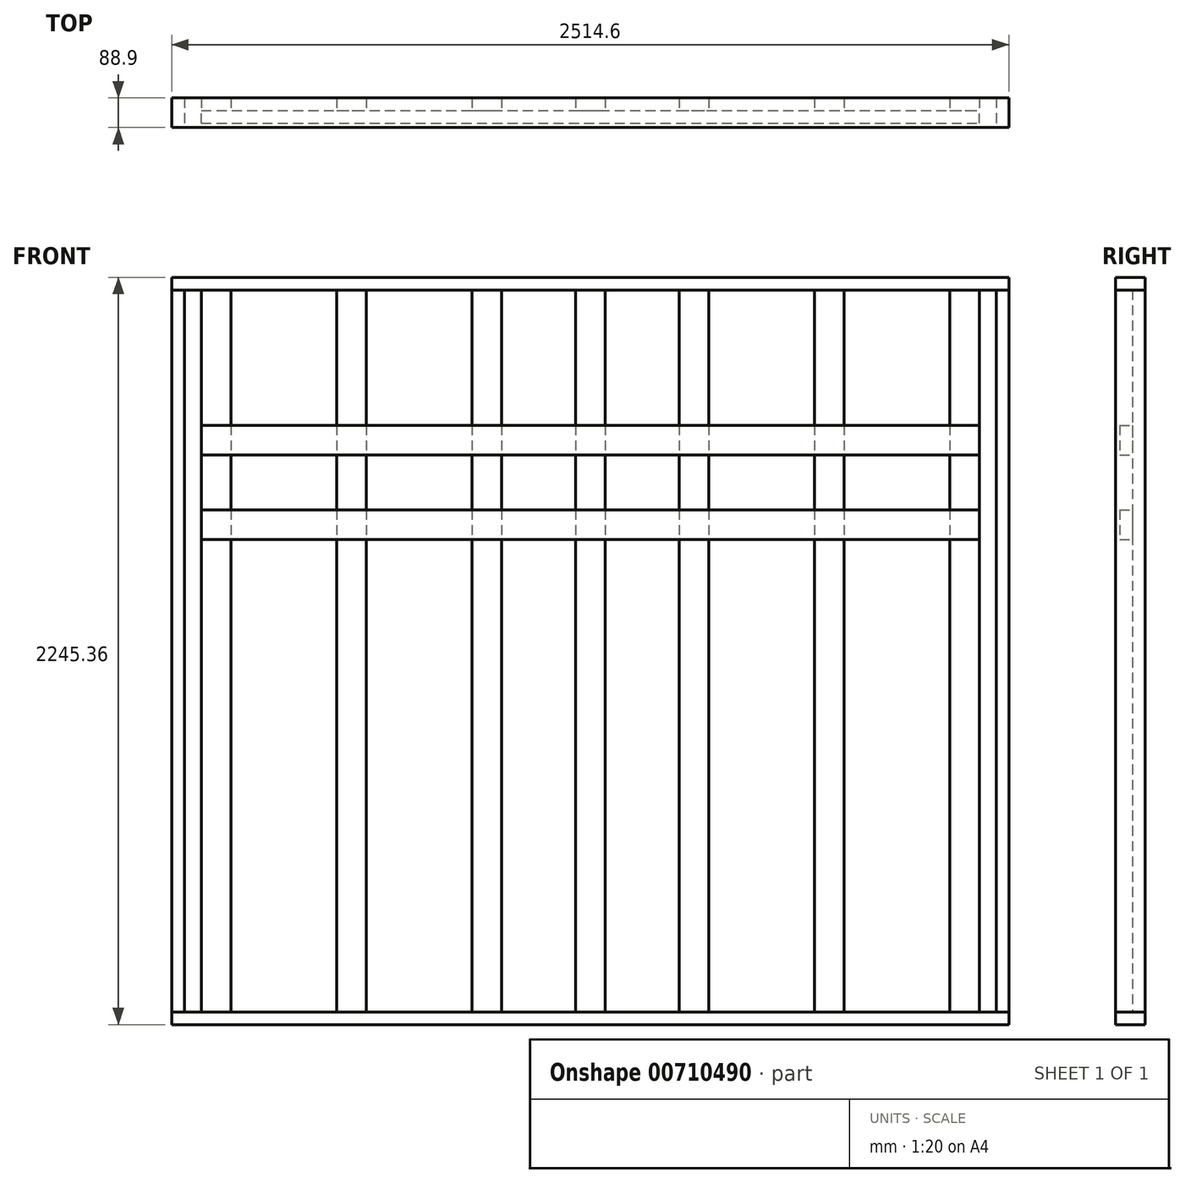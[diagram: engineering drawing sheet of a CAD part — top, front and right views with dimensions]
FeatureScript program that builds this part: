
annotation { "Feature Type Name" : "Feature", "Feature Type Description" : "" }
export const myFeature = defineFeature(function(context is Context, id is Id, definition is map)
    precondition{}
    {
        {
            var Q0;
            Q0=qCreatedBy(makeId("Top.planeOp"),FACE);
            var sketch = newSketch(context, id + "F0", { "sketchPlane" : qUnion([Q0])});
            skLineSegment(sketch, "E0.bottom", {"start": v(1257.3, 44.45) * mm, "end": v(-1257.3, 44.45) * mm});
            skLineSegment(sketch, "E0.top", {"start": v(1257.3, -44.45) * mm, "end": v(-1257.3, -44.45) * mm});
            skLineSegment(sketch, "E0.left", {"start": v(1257.3, 44.45) * mm, "end": v(1257.3, -44.45) * mm});
            skLineSegment(sketch, "E0.right", {"start": v(-1257.3, 44.45) * mm, "end": v(-1257.3, -44.45) * mm});
            skPoint(sketch, "E0.middle", {"position": v(0, 0) * mm});
            skSolve(sketch);
        }
        {
            var Q0;
            Q0=qSketchRegion(id+"F0",true);
            extrude(context, id + "F1", {"entities" : qUnion([Q0]), "depth" : 38.1 * mm, "offsetDistance" : 25.4 * mm});
        }
        {
            var Q0;
            Q0=makeQuery(id+"F1.opExtrude","CAP_FACE",FACE,{"disambiguationData":[OSD([sQuery(id+"F0.wireOp",EDGE,"E0.bottom"),sQuery(id+"F0.wireOp",EDGE,"E0.top"),sQuery(id+"F0.wireOp",EDGE,"E0.left"),sQuery(id+"F0.wireOp",EDGE,"E0.right")])],"isStart":false});
            var sketch = newSketch(context, id + "F2", { "sketchPlane" : qUnion([Q0])});
            skLineSegment(sketch, "E1.bottom", {"start": v(-1257.3, 44.45) * mm, "end": v(-1219.2, 44.45) * mm});
            skLineSegment(sketch, "E1.top", {"start": v(-1257.3, -44.45) * mm, "end": v(-1219.2, -44.45) * mm});
            skLineSegment(sketch, "E1.left", {"start": v(-1257.3, 44.45) * mm, "end": v(-1257.3, -44.45) * mm});
            skLineSegment(sketch, "E1.right", {"start": v(-1219.2, 44.45) * mm, "end": v(-1219.2, -44.45) * mm});
            skSolve(sketch);
        }
        {
            var Q0;
            Q0=makeQuery(id+"F2.imprint","IMPRINT",FACE,{"disambiguationData":[TD([[makeQuery(id+"F2.imprint","IMPRINT",EDGE,{"derivedFrom":sQuery(id+"F2.wireOp",EDGE,"E1.bottom")}),1.0]])]});
            extrude(context, id + "F3", {"entities" : qUnion([Q0]), "depth" : 2169.16 * mm, "offsetDistance" : 25.4 * mm});
        }
        {
            var Q0;
            Q0=makeQuery(id+"F3.opExtrude","SWEPT_BODY",BODY,{"disambiguationData":[OSD([sQuery(id+"F2.wireOp",EDGE,"E1.bottom"),sQuery(id+"F2.wireOp",EDGE,"E1.top"),sQuery(id+"F2.wireOp",EDGE,"E1.left"),sQuery(id+"F2.wireOp",EDGE,"E1.right")])]});
            var Q1;
            Q1=qCreatedBy(makeId("Right.planeOp"),FACE);
            mirror(context, id + "F4", {"entities" : qUnion([Q0]), "mirrorPlane" : qUnion([Q1])});
        }
        {
            var Q0;
            Q0=makeQuery(id+"F1.opExtrude","CAP_FACE",FACE,{"disambiguationData":[OSD([sQuery(id+"F0.wireOp",EDGE,"E0.bottom"),sQuery(id+"F0.wireOp",EDGE,"E0.top"),sQuery(id+"F0.wireOp",EDGE,"E0.left"),sQuery(id+"F0.wireOp",EDGE,"E0.right")])],"isStart":false});
            var sketch = newSketch(context, id + "F5", { "sketchPlane" : qUnion([Q0])});
            skLineSegment(sketch, "E2.bottom", {"start": v(-1168.4, 44.45) * mm, "end": v(-1079.5, 44.45) * mm});
            skLineSegment(sketch, "E2.top", {"start": v(-1168.4, 6.35) * mm, "end": v(-1079.5, 6.35) * mm});
            skLineSegment(sketch, "E2.left", {"start": v(-1168.4, 44.45) * mm, "end": v(-1168.4, 6.35) * mm});
            skLineSegment(sketch, "E2.right", {"start": v(-1079.5, 44.45) * mm, "end": v(-1079.5, 6.35) * mm});
            skLineSegment(sketch, "E3", {"start": v(-1123.95, 44.45) * mm, "end": v(-1123.95, 6.35) * mm, "construction": true});
            skLineSegment(sketch, "E4.bottom", {"start": v(-44.45, 44.45) * mm, "end": v(44.45, 44.45) * mm});
            skLineSegment(sketch, "E4.top", {"start": v(-44.45, 6.35) * mm, "end": v(44.45, 6.35) * mm});
            skLineSegment(sketch, "E4.left", {"start": v(-44.45, 44.45) * mm, "end": v(-44.45, 6.35) * mm});
            skLineSegment(sketch, "E4.right", {"start": v(44.45, 44.45) * mm, "end": v(44.45, 6.35) * mm});
            skLineSegment(sketch, "E5", {"start": v(0, 44.45) * mm, "end": v(0, 6.35) * mm, "construction": true});
            skLineSegment(sketch, "E6.bottom", {"start": v(-762, 44.45) * mm, "end": v(-673.1, 44.45) * mm});
            skLineSegment(sketch, "E6.top", {"start": v(-762, 6.35) * mm, "end": v(-673.1, 6.35) * mm});
            skLineSegment(sketch, "E6.left", {"start": v(-762, 44.45) * mm, "end": v(-762, 6.35) * mm});
            skLineSegment(sketch, "E6.right", {"start": v(-673.1, 44.45) * mm, "end": v(-673.1, 6.35) * mm});
            skLineSegment(sketch, "E7", {"start": v(-717.55, 44.45) * mm, "end": v(-717.55, 6.35) * mm, "construction": true});
            skLineSegment(sketch, "E8.bottom", {"start": v(-355.6, 44.45) * mm, "end": v(-266.7, 44.45) * mm});
            skLineSegment(sketch, "E8.top", {"start": v(-355.6, 6.35) * mm, "end": v(-266.7, 6.35) * mm});
            skLineSegment(sketch, "E8.left", {"start": v(-355.6, 44.45) * mm, "end": v(-355.6, 6.35) * mm});
            skLineSegment(sketch, "E8.right", {"start": v(-266.7, 44.45) * mm, "end": v(-266.7, 6.35) * mm});
            skLineSegment(sketch, "E9", {"start": v(-311.15, 44.45) * mm, "end": v(-311.15, 6.35) * mm, "construction": true});
            skLineSegment(sketch, "E10.bottom", {"start": v(266.7, 44.45) * mm, "end": v(355.6, 44.45) * mm});
            skLineSegment(sketch, "E10.top", {"start": v(266.7, 6.35) * mm, "end": v(355.6, 6.35) * mm});
            skLineSegment(sketch, "E10.left", {"start": v(266.7, 44.45) * mm, "end": v(266.7, 6.35) * mm});
            skLineSegment(sketch, "E10.right", {"start": v(355.6, 44.45) * mm, "end": v(355.6, 6.35) * mm});
            skLineSegment(sketch, "E11", {"start": v(311.15, 44.45) * mm, "end": v(311.15, 6.35) * mm, "construction": true});
            skLineSegment(sketch, "E12.bottom", {"start": v(673.1, 44.45) * mm, "end": v(762, 44.45) * mm});
            skLineSegment(sketch, "E12.top", {"start": v(673.1, 6.35) * mm, "end": v(762, 6.35) * mm});
            skLineSegment(sketch, "E12.left", {"start": v(673.1, 44.45) * mm, "end": v(673.1, 6.35) * mm});
            skLineSegment(sketch, "E12.right", {"start": v(762, 44.45) * mm, "end": v(762, 6.35) * mm});
            skLineSegment(sketch, "E13", {"start": v(717.55, 44.45) * mm, "end": v(717.55, 6.35) * mm, "construction": true});
            skLineSegment(sketch, "E14.bottom", {"start": v(1079.5, 44.45) * mm, "end": v(1168.4, 44.45) * mm});
            skLineSegment(sketch, "E14.top", {"start": v(1079.5, 6.35) * mm, "end": v(1168.4, 6.35) * mm});
            skLineSegment(sketch, "E14.left", {"start": v(1079.5, 44.45) * mm, "end": v(1079.5, 6.35) * mm});
            skLineSegment(sketch, "E14.right", {"start": v(1168.4, 44.45) * mm, "end": v(1168.4, 6.35) * mm});
            skLineSegment(sketch, "E15", {"start": v(1123.95, 44.45) * mm, "end": v(1123.95, 6.35) * mm, "construction": true});
            skSolve(sketch);
        }
        {
            var Q0;
            Q0=qSketchRegion(id+"F5",true);
            var Q1;
            Q1=makeQuery(id+"F3.opExtrude","CAP_FACE",FACE,{"disambiguationData":[OSD([sQuery(id+"F2.wireOp",EDGE,"E1.bottom"),sQuery(id+"F2.wireOp",EDGE,"E1.top"),sQuery(id+"F2.wireOp",EDGE,"E1.left"),sQuery(id+"F2.wireOp",EDGE,"E1.right")])],"isStart":false});
            extrude(context, id + "F6", {"entities" : qUnion([Q0]), "endBound" : BoundingType.UP_TO_SURFACE, "depth" : 25.4 * mm, "endBoundEntityFace" : qUnion([Q1]), "offsetDistance" : 25.4 * mm});
        }
        {
            var Q0;
            Q0=makeQuery(id+"F3.opExtrude","CAP_FACE",FACE,{"disambiguationData":[OSD([sQuery(id+"F2.wireOp",EDGE,"E1.bottom"),sQuery(id+"F2.wireOp",EDGE,"E1.top"),sQuery(id+"F2.wireOp",EDGE,"E1.left"),sQuery(id+"F2.wireOp",EDGE,"E1.right")])],"isStart":false});
            var sketch = newSketch(context, id + "F7", { "sketchPlane" : qUnion([Q0])});
            skLineSegment(sketch, "E16.bottom", {"start": v(-1257.3, 44.45) * mm, "end": v(1257.3, 44.45) * mm});
            skLineSegment(sketch, "E16.top", {"start": v(-1257.3, -44.45) * mm, "end": v(1257.3, -44.45) * mm});
            skLineSegment(sketch, "E16.left", {"start": v(-1257.3, 44.45) * mm, "end": v(-1257.3, -44.45) * mm});
            skLineSegment(sketch, "E16.right", {"start": v(1257.3, 44.45) * mm, "end": v(1257.3, -44.45) * mm});
            skSolve(sketch);
        }
        {
            var Q0;
            Q0=qSketchRegion(id+"F7",true);
            extrude(context, id + "F8", {"entities" : qUnion([Q0]), "depth" : 38.1 * mm, "offsetDistance" : 25.4 * mm});
        }
        {
            var Q0;
            Q0=makeQuery(id+"F6.opExtrude","SWEPT_FACE",FACE,{"disambiguationData":[OSD([sQuery(id+"F5.wireOp",EDGE,"E2.top")])]});
            var sketch = newSketch(context, id + "F9", { "sketchPlane" : qUnion([Q0])});
            skLineSegment(sketch, "E17.bottom", {"start": v(-1168.4, 1800.86) * mm, "end": v(1168.4, 1800.86) * mm});
            skLineSegment(sketch, "E17.top", {"start": v(-1168.4, 1711.96) * mm, "end": v(1168.4, 1711.96) * mm});
            skLineSegment(sketch, "E17.left", {"start": v(-1168.4, 1800.86) * mm, "end": v(-1168.4, 1711.96) * mm});
            skLineSegment(sketch, "E17.right", {"start": v(1168.4, 1800.86) * mm, "end": v(1168.4, 1711.96) * mm});
            skLineSegment(sketch, "E18.bottom", {"start": v(-1168.4, 1546.86) * mm, "end": v(1168.4, 1546.86) * mm});
            skLineSegment(sketch, "E18.top", {"start": v(-1168.4, 1457.96) * mm, "end": v(1168.4, 1457.96) * mm});
            skLineSegment(sketch, "E18.left", {"start": v(-1168.4, 1546.86) * mm, "end": v(-1168.4, 1457.96) * mm});
            skLineSegment(sketch, "E18.right", {"start": v(1168.4, 1546.86) * mm, "end": v(1168.4, 1457.96) * mm});
            skSolve(sketch);
        }
        {
            var Q0;
            Q0=qSketchRegion(id+"F9",true);
            extrude(context, id + "F10", {"entities" : qUnion([Q0]), "depth" : 38.1 * mm, "offsetDistance" : 25.4 * mm});
        }
    });
